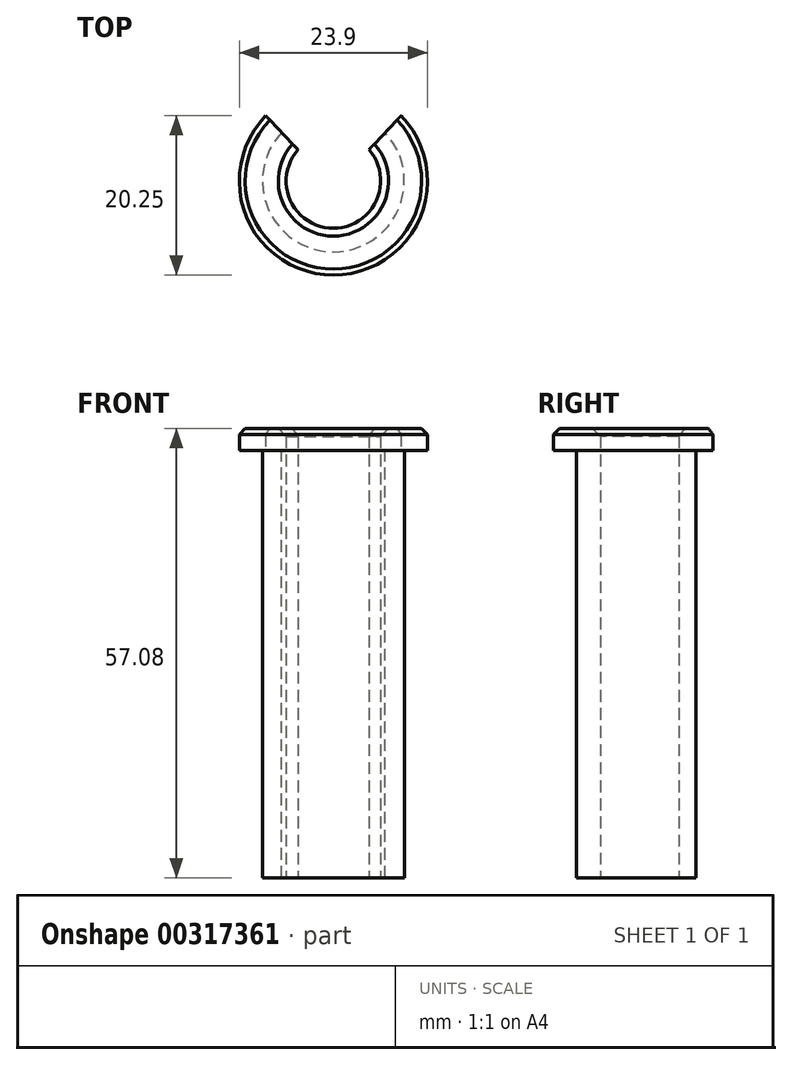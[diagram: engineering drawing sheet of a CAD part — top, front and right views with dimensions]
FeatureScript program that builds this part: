
annotation { "Feature Type Name" : "Feature", "Feature Type Description" : "" }
export const myFeature = defineFeature(function(context is Context, id is Id, definition is map)
    precondition{}
    {
        {
            var Q0;
            Q0=qCreatedBy(makeId("Top.planeOp"),FACE);
            var sketch = newSketch(context, id + "F0", { "sketchPlane" : qUnion([Q0])});
            skArc(sketch, "E0", {"start": v(-4.5, 3.97) * mm, "mid": v(0, -6) * mm, "end": v(4.5, 3.97) * mm});
            skArc(sketch, "E1", {"start": v(-8.6, 8.3) * mm, "mid": v(0, -11.95) * mm, "end": v(8.6, 8.3) * mm});
            skLineSegment(sketch, "E2", {"start": v(-4.5, 3.97) * mm, "end": v(-8.6, 8.3) * mm});
            skLineSegment(sketch, "E3", {"start": v(4.5, 3.97) * mm, "end": v(8.6, 8.3) * mm});
            skSolve(sketch);
        }
        {
            var Q0;
            Q0 = qSketchRegion(id + "F0", true);
            extrude(context, id + "F1", {"entities" : qUnion([Q0]), "depth" : 2.78 * mm, "offsetDistance" : 25 * mm});
        }
        {
            var Q0;
            Q0=makeQuery(id+"F1.opExtrude","CAP_FACE",FACE,{"disambiguationData":[OSD([sQuery(id+"F0.wireOp",EDGE,"E0"),sQuery(id+"F0.wireOp",EDGE,"E1"),sQuery(id+"F0.wireOp",EDGE,"E2"),sQuery(id+"F0.wireOp",EDGE,"E3")])],"isStart":true});
            var sketch = newSketch(context, id + "F2", { "sketchPlane" : qUnion([Q0])});
            skArc(sketch, "E4", {"start": v(4.5, -3.97) * mm, "mid": v(0, 6) * mm, "end": v(-4.5, -3.97) * mm});
            skLineSegment(sketch, "E5", {"start": v(4.5, -3.97) * mm, "end": v(6.57, -6.15) * mm});
            skLineSegment(sketch, "E6", {"start": v(-4.5, -3.97) * mm, "end": v(-6.57, -6.15) * mm});
            skArc(sketch, "E7", {"start": v(6.57, -6.15) * mm, "mid": v(0, 9) * mm, "end": v(-6.57, -6.15) * mm});
            skSolve(sketch);
        }
        {
            var Q0;
            Q0 = qSketchRegion(id + "F2", true);
            extrude(context, id + "F3", {"entities" : qUnion([Q0]), "operationType" : NewBodyOperationType.ADD, "depth" : 54.3 * mm, "offsetDistance" : 25 * mm});
        }
        {
            var Q0;
            Q0=makeQuery(id+"F1.opExtrude","CAP_EDGE",EDGE,{"disambiguationData":[OSD([sQuery(id+"F0.wireOp",EDGE,"E1")])],"isStart":false});
            chamfer(context, id + "F4", {"entities" : qUnion([Q0]), "width" : 0.75 * mm, "tangentPropagation" : true});
        }
        {
            var Q0;
            Q0=makeQuery(id+"F1.opExtrude","CAP_EDGE",EDGE,{"disambiguationData":[OSD([sQuery(id+"F0.wireOp",EDGE,"E0")])],"isStart":false});
            chamfer(context, id + "F5", {"entities" : qUnion([Q0]), "width" : 1 * mm, "tangentPropagation" : true});
        }
    });
